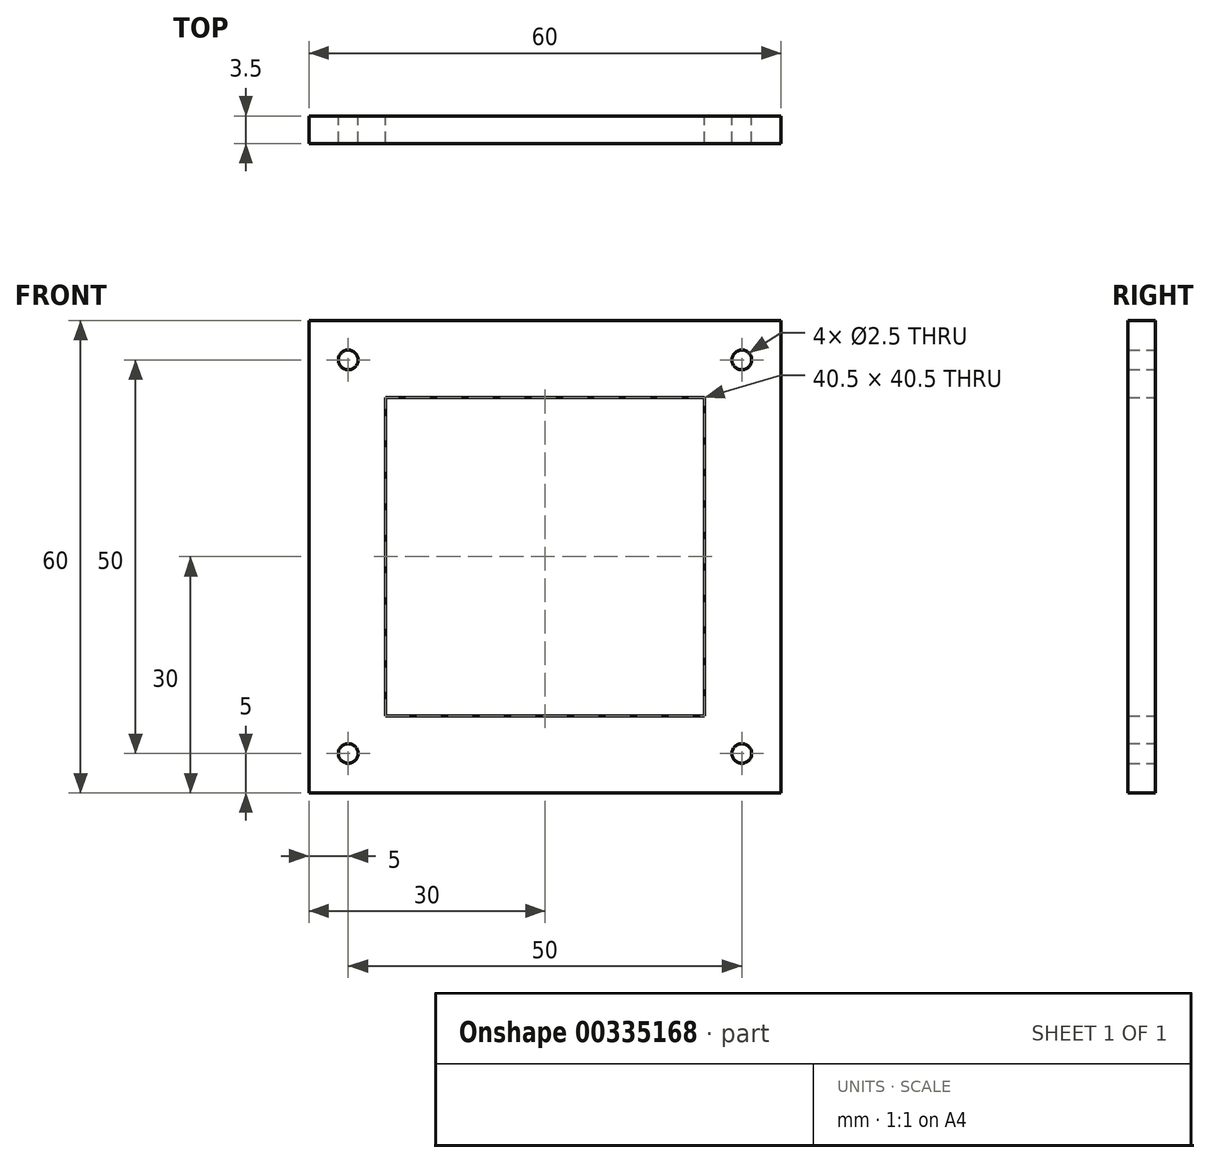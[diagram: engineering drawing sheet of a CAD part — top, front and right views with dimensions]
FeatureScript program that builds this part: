
annotation { "Feature Type Name" : "Feature", "Feature Type Description" : "" }
export const myFeature = defineFeature(function(context is Context, id is Id, definition is map)
    precondition{}
    {
        {
            var Q0;
            Q0=qCreatedBy(makeId("Front.planeOp"),FACE);
            var sketch = newSketch(context, id + "F0", { "sketchPlane" : qUnion([Q0])});
            skLineSegment(sketch, "E0.bottom", {"start": v(20.25, -20.25) * mm, "end": v(-20.25, -20.25) * mm});
            skLineSegment(sketch, "E0.top", {"start": v(20.25, 20.25) * mm, "end": v(-20.25, 20.25) * mm});
            skLineSegment(sketch, "E0.left", {"start": v(20.25, -20.25) * mm, "end": v(20.25, 20.25) * mm});
            skLineSegment(sketch, "E0.right", {"start": v(-20.25, -20.25) * mm, "end": v(-20.25, 20.25) * mm});
            skPoint(sketch, "E0.middle", {"position": v(0, 0) * mm});
            skLineSegment(sketch, "E1.bottom", {"start": v(30, -30) * mm, "end": v(-30, -30) * mm});
            skLineSegment(sketch, "E1.top", {"start": v(30, 30) * mm, "end": v(-30, 30) * mm});
            skLineSegment(sketch, "E1.left", {"start": v(30, -30) * mm, "end": v(30, 30) * mm});
            skLineSegment(sketch, "E1.right", {"start": v(-30, -30) * mm, "end": v(-30, 30) * mm});
            skCircle(sketch, "E2", {"center": v(0, 0) * mm, "radius": 12.5 * mm});
            skCircle(sketch, "E3", {"center": v(-25, 25) * mm, "radius": 1.25 * mm});
            skCircle(sketch, "E4", {"center": v(-25, -25) * mm, "radius": 1.25 * mm});
            skCircle(sketch, "E5", {"center": v(25, 25) * mm, "radius": 1.25 * mm});
            skCircle(sketch, "E6", {"center": v(25, -25) * mm, "radius": 1.25 * mm});
            skSolve(sketch);
        }
        {
            var Q0;
            Q0=makeQuery(id+"F0.imprint","IMPRINT",FACE,{"disambiguationData":[TD([[makeQuery(id+"F0.imprint","IMPRINT",EDGE,{"derivedFrom":sQuery(id+"F0.wireOp",EDGE,"E0.bottom")}),1.0]])]});
            extrude(context, id + "F1", {"entities" : qUnion([Q0]), "depth" : 3.5 * mm});
        }
    });
